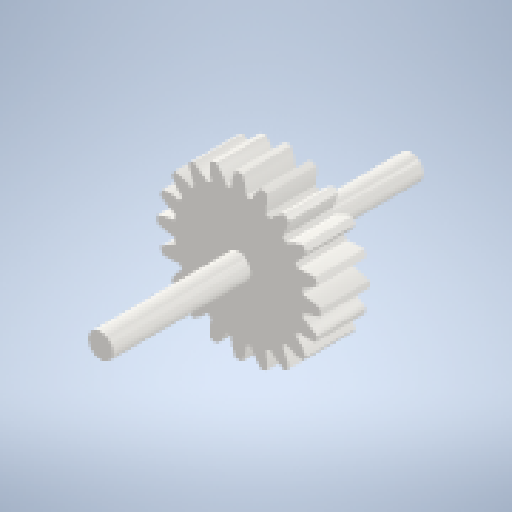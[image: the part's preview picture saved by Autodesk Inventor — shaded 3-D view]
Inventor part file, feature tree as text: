
AUTODESK INVENTOR PART (.ipt)
format: ipt  version: 2023.2 (Build 272271000, 271)  size: 409,600 bytes
history: native  units: mm (DEFAULTED — no unit token found)
features: sketch x4, plane x3, other x3, extrude x2
ambient origin geometry x8: Origin, YZ Plane, XZ Plane, XY Plane, X Axis, Y Axis, Z Axis, Center Point
bodies: Solid1 (feature_tree)
feature tree (12):
  extrude  "Extrusion1"  Depth=20.0mm TaperAngle=0.0deg
  plane  "Work Plane2"
  plane  "Work Plane8"
  plane  "Work Plane9"
  other  "Spur Gear"
  sketch  "Sketch3"  dims[d16=90.0mm]
  extrude  "Extrusion2"  Depth=10.0mm TaperAngle=0.0deg
  sketch  "Sketch1"  dims[d0=66.0mm d1=20.0mm d2=0.0mm]
  sketch  "Sketch2"  dims[d3=60.0mm d4=10.0mm d5=0.0mm]
  other  "Srf1"
  sketch  "Sketch4"  dims[d17=0.0mm d34=1.570796mm d39=0.0mm d41=0.0mm d43=90.0mm d46=90.0mm d47=0.0mm d48=0.0mm d49=10.0mm d50=50.0mm d51=0.0mm d52=76.0mm d53=0.0mm]
  other  "Pitch Diameter"
